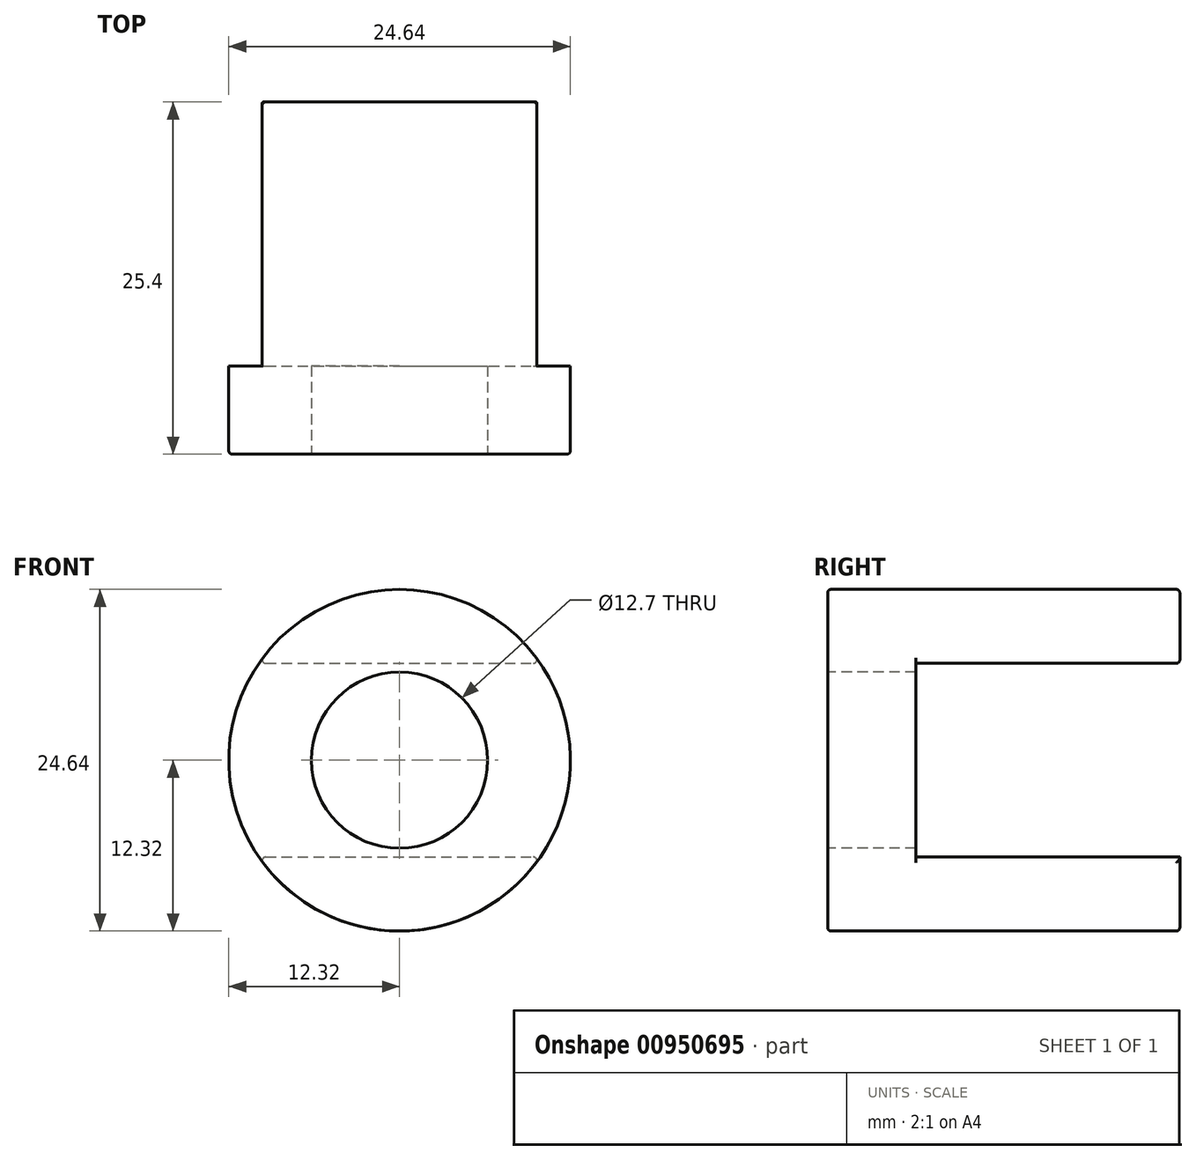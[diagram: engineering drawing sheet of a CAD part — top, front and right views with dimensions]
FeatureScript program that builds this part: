
annotation { "Feature Type Name" : "Feature", "Feature Type Description" : "" }
export const myFeature = defineFeature(function(context is Context, id is Id, definition is map)
    precondition{}
    {
        {
            var Q0;
            Q0=qCreatedBy(makeId("Front.planeOp"),FACE);
            var sketch = newSketch(context, id + "F0", { "sketchPlane" : qUnion([Q0])});
            skCircle(sketch, "E0", {"center": v(0, 0) * mm, "radius": 12.32 * mm});
            skSolve(sketch);
        }
        {
            var Q0;
            Q0 = qSketchRegion(id + "F0", true);
            extrude(context, id + "F1", {"entities" : qUnion([Q0]), "depth" : 25.4 * mm, "offsetDistance" : 25.4 * mm});
        }
        {
            var Q0;
            Q0=makeQuery(id+"F1.opExtrude","CAP_FACE",FACE,{"disambiguationData":[OSD([sQuery(id+"F0.wireOp",EDGE,"E0")])],"isStart":true});
            var sketch = newSketch(context, id + "F2", { "sketchPlane" : qUnion([Q0])});
            skLineSegment(sketch, "E1.bottom", {"start": v(30.22, -6.99) * mm, "end": v(-30.22, -6.99) * mm});
            skLineSegment(sketch, "E1.top", {"start": v(30.22, 6.99) * mm, "end": v(-30.22, 6.99) * mm});
            skLineSegment(sketch, "E1.left", {"start": v(30.22, -6.99) * mm, "end": v(30.22, 6.99) * mm});
            skLineSegment(sketch, "E1.right", {"start": v(-30.22, -6.99) * mm, "end": v(-30.22, 6.99) * mm});
            skPoint(sketch, "E1.middle", {"position": v(0, 0) * mm});
            skSolve(sketch);
        }
        {
            var Q0;
            Q0 = qSketchRegion(id + "F2", true);
            extrude(context, id + "F3", {"entities" : qUnion([Q0]), "operationType" : NewBodyOperationType.REMOVE, "oppositeDirection" : true, "depth" : 19.05 * mm, "offsetDistance" : 25.4 * mm});
        }
        {
            var Q0;
            Q0=makeQuery(id+"F1.opExtrude","CAP_FACE",FACE,{"disambiguationData":[OSD([sQuery(id+"F0.wireOp",EDGE,"E0")])],"isStart":false});
            var sketch = newSketch(context, id + "F4", { "sketchPlane" : qUnion([Q0])});
            skCircle(sketch, "E2", {"center": v(0, 0) * mm, "radius": 6.35 * mm});
            skSolve(sketch);
        }
        {
            var Q0;
            Q0 = qSketchRegion(id + "F4", true);
            extrude(context, id + "F5", {"entities" : qUnion([Q0]), "operationType" : NewBodyOperationType.REMOVE, "oppositeDirection" : true, "depth" : 25.4 * mm, "offsetDistance" : 25.4 * mm});
        }
        {
            var Q0;
            Q0=makeQuery(id+"F3.boolean.opBoolean","INTERSECT",EDGE,{"disambiguationData":[OD(1.0)],"derivedFrom":[makeQuery(id+"F1.opExtrude","SWEPT_FACE",FACE,{"disambiguationData":[OSD([sQuery(id+"F0.wireOp",EDGE,"E0")])]}),makeQuery(id+"F3.opExtrude","SWEPT_FACE",FACE,{"disambiguationData":[OSD([sQuery(id+"F2.wireOp",EDGE,"E1.top")])]})]});
            var Q1;
            Q1=makeQuery(id+"F3.boolean.opBoolean","COPY",EDGE,{"derivedFrom":makeQuery(id+"F3.opExtrude","CAP_EDGE",EDGE,{"disambiguationData":[OSD([sQuery(id+"F2.wireOp",EDGE,"E1.top")])],"isStart":true})});
            var Q2;
            {var subQ0=sQuery(id+"F0.wireOp",EDGE,"E0");Q2=makeQuery(id+"F3.boolean.opBoolean","SPLIT",EDGE,{"disambiguationData":[TD([makeQuery(id+"F3.opExtrude","SWEPT_FACE",FACE,{"disambiguationData":[OSD([sQuery(id+"F2.wireOp",EDGE,"E1.top")])]})])],"derivedFrom":makeQuery(id+"F1.opExtrude","CAP_EDGE",EDGE,{"disambiguationData":[OSD([subQ0])],"isStart":true})});}
            var Q3;
            Q3=makeQuery(id+"F3.boolean.opBoolean","INTERSECT",EDGE,{"disambiguationData":[OD(0.0)],"derivedFrom":[makeQuery(id+"F1.opExtrude","SWEPT_FACE",FACE,{"disambiguationData":[OSD([sQuery(id+"F0.wireOp",EDGE,"E0")])]}),makeQuery(id+"F3.opExtrude","SWEPT_FACE",FACE,{"disambiguationData":[OSD([sQuery(id+"F2.wireOp",EDGE,"E1.top")])]})]});
            var Q4;
            Q4=makeQuery(id+"F3.boolean.opBoolean","INTERSECT",EDGE,{"disambiguationData":[OD(1.0)],"derivedFrom":[makeQuery(id+"F1.opExtrude","SWEPT_FACE",FACE,{"disambiguationData":[OSD([sQuery(id+"F0.wireOp",EDGE,"E0")])]}),makeQuery(id+"F3.opExtrude","SWEPT_FACE",FACE,{"disambiguationData":[OSD([sQuery(id+"F2.wireOp",EDGE,"E1.bottom")])]})]});
            var Q5;
            Q5=makeQuery(id+"F3.boolean.opBoolean","INTERSECT",EDGE,{"disambiguationData":[OD(0.0)],"derivedFrom":[makeQuery(id+"F1.opExtrude","SWEPT_FACE",FACE,{"disambiguationData":[OSD([sQuery(id+"F0.wireOp",EDGE,"E0")])]}),makeQuery(id+"F3.opExtrude","SWEPT_FACE",FACE,{"disambiguationData":[OSD([sQuery(id+"F2.wireOp",EDGE,"E1.bottom")])]})]});
            var Q6;
            Q6=makeQuery(id+"F3.boolean.opBoolean","COPY",EDGE,{"derivedFrom":makeQuery(id+"F3.opExtrude","CAP_EDGE",EDGE,{"disambiguationData":[OSD([sQuery(id+"F2.wireOp",EDGE,"E1.bottom")])],"isStart":true})});
            var Q7;
            {var subQ0=sQuery(id+"F0.wireOp",EDGE,"E0");Q7=makeQuery(id+"F3.boolean.opBoolean","SPLIT",EDGE,{"disambiguationData":[TD([makeQuery(id+"F3.opExtrude","SWEPT_FACE",FACE,{"disambiguationData":[OSD([sQuery(id+"F2.wireOp",EDGE,"E1.bottom")])]})])],"derivedFrom":makeQuery(id+"F1.opExtrude","CAP_EDGE",EDGE,{"disambiguationData":[OSD([subQ0])],"isStart":true})});}
            var Q8;
            Q8=makeQuery(id+"F1.opExtrude","CAP_EDGE",EDGE,{"disambiguationData":[OSD([sQuery(id+"F0.wireOp",EDGE,"E0")])],"isStart":false});
            fillet(context, id + "F6", {"entities" : qUnion([Q0, Q1, Q2, Q3, Q4, Q5, Q6, Q7, Q8]), "radius" : 0.25 * mm, "tangentPropagation" : true, "allowEdgeOverflow" : false});
        }
    });
